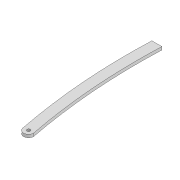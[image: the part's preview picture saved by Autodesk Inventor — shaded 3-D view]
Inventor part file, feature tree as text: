
AUTODESK INVENTOR PART (.ipt)
format: ipt  version: 2022 (Build 260153000, 153)  size: 107,520 bytes
history: native  units: mm
features: extrude x2, sketch x2
ambient origin geometry x8: Origin, YZ Plane, XZ Plane, XY Plane, X Axis, Y Axis, Z Axis, Center Point
bodies: Solid1 (feature_tree)
feature tree (4):
  extrude  "Extrusion1"  Depth=3.3mm
  extrude  "Extrusion2"  Depth=10.0mm
  sketch  "Sketch1"  dims[d0=3.3mm d1=3.3mm]
  sketch  "Sketch2"  dims[d2=10.0mm d3=288.984mm d6=3.0mm d7=0.0mm d14=3.3mm d15=231.585mm d18=600.0mm d19=600.0mm d20=10.0mm d21=0.0mm]
